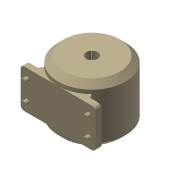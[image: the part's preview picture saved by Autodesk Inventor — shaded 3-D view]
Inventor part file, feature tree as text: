
AUTODESK INVENTOR PART (.ipt)
format: ipt  version: 2022.5 (Build 265521000, 521)  size: 217,600 bytes
history: native  units: mm
features: extrude x6, sketch x2, projected_geometry x2, chamfer x1, fillet x1, other x1
ambient origin geometry x8: Origin, YZ Plane, XZ Plane, XY Plane, X Axis, Y Axis, Z Axis, Center Point
bodies: Solid1 (feature_tree)
feature tree (13):
  extrude  "Extrusion1"  Depth=30.0mm TaperAngle=0.0deg
  extrude  "Extrusion2"  Depth=4.0mm
  chamfer  "Chamfer1"  Angle=60.0deg  [1 undecoded]
  extrude  "Extrusion3"  Depth=20.0mm TaperAngle=0.0deg
  extrude  "Extrusion4"  Depth=3.0mm TaperAngle=45.0deg
  fillet  "Fillet2"  Radius=6.0mm
  extrude  "Extrusion5"  Depth=8.0mm TaperAngle=0.0deg
  other  "Work Axis1"
  extrude  "Extrusion6"  TaperAngle=0.0deg  [1 undecoded]
  sketch  "Sketch2"  dims[d0=35.0mm d1=30.0mm d2=0.0mm]
  projected_geometry  "Projected Loop1"
  projected_geometry  "Projected Loop2"
  sketch  "Sketch6"  dims[d4=3.0mm d5=4.0mm d6=60.0deg d7=20.0mm d8=0.0mm d9=3.0mm d10=2.0mm d11=45.0deg d12=6.0mm d13=8.0mm d14=0.0mm d16=0.0mm d17=4.0mm d18=2.0mm d19=5.0mm d20=5.0mm d22=10.0mm d23=0.0mm d24=2.0mm d26=4.0mm d29=1.5mm d30=0.0mm d31=35.0mm d32=39.0mm d33=16.0mm d34=16.0mm d35=2.5mm d36=4.0mm d37=4.0mm d38=4.0mm d39=4.0mm d40=0.0mm]
note: 2 required parameter values undecoded (feature->parameter linkage not recoverable at this tier; creation-order binding heuristic only, values carry confidence <= 0.55)
